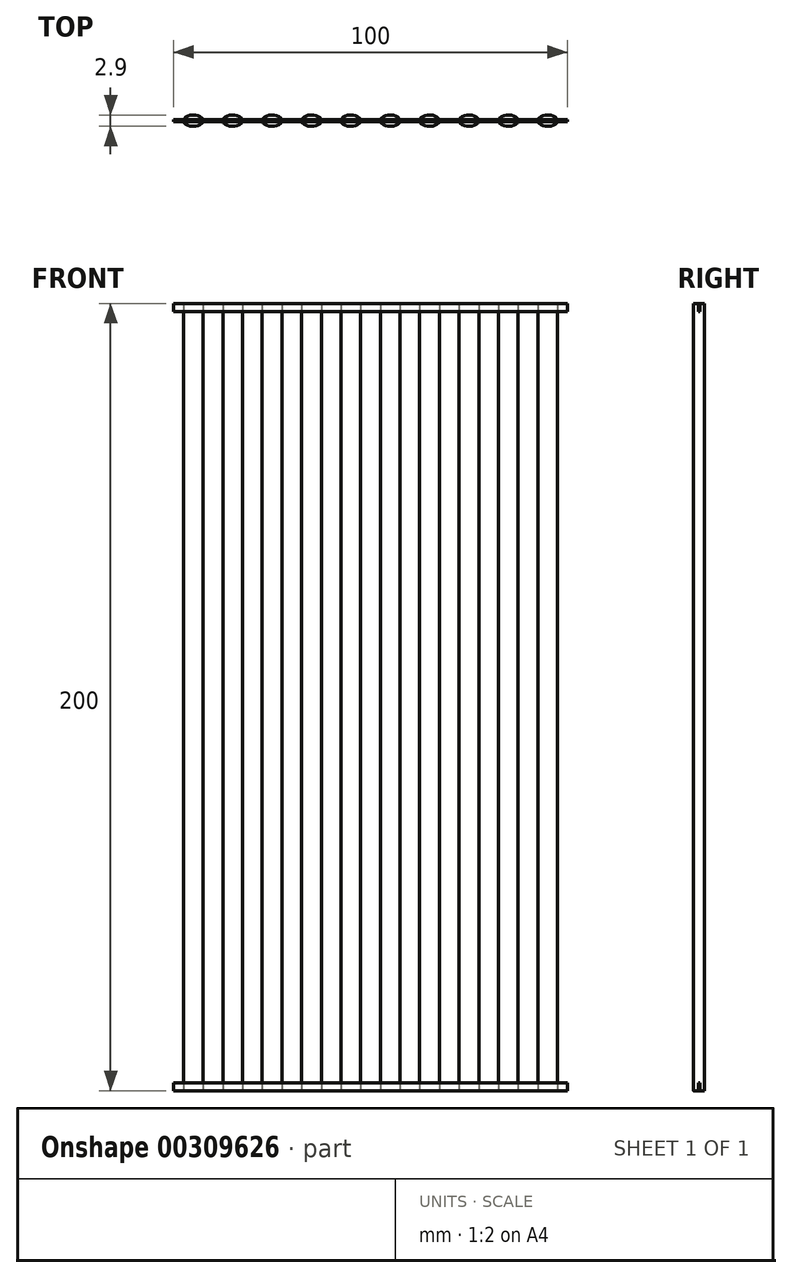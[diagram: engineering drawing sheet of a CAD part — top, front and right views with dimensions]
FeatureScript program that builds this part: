
annotation { "Feature Type Name" : "Feature", "Feature Type Description" : "" }
export const myFeature = defineFeature(function(context is Context, id is Id, definition is map)
    precondition{}
    {
        {
            var Q0;
            Q0=qCreatedBy(makeId("Top.planeOp"),FACE);
            var sketch = newSketch(context, id + "F0", { "sketchPlane" : qUnion([Q0])});
            skEllipse(sketch, "E0", {"center": v(-5, 0) * mm, "majorRadius": 2.5 * mm, "minorRadius": 1.45 * mm, "majorAxis": v(1, 0)});
            skEllipse(sketch, "E1", {"center": v(-15, 0) * mm, "majorRadius": 2.5 * mm, "minorRadius": 1.45 * mm, "majorAxis": v(1, 0)});
            skEllipse(sketch, "E2", {"center": v(-25, 0) * mm, "majorRadius": 2.5 * mm, "minorRadius": 1.45 * mm, "majorAxis": v(1, 0)});
            skEllipse(sketch, "E3", {"center": v(-35, 0) * mm, "majorRadius": 2.5 * mm, "minorRadius": 1.45 * mm, "majorAxis": v(1, 0)});
            skEllipse(sketch, "E4", {"center": v(-45, 0) * mm, "majorRadius": 2.5 * mm, "minorRadius": 1.45 * mm, "majorAxis": v(1, 0)});
            skSolve(sketch);
        }
        {
            var Q0;
            Q0=makeQuery(id+"F0.imprint","IMPRINT",FACE,{"disambiguationData":[TD([[makeQuery(id+"F0.imprint","IMPRINT",EDGE,{"derivedFrom":sQuery(id+"F0.wireOp",EDGE,"E4")}),1.0]])]});
            var Q1;
            Q1=makeQuery(id+"F0.imprint","IMPRINT",FACE,{"disambiguationData":[TD([[makeQuery(id+"F0.imprint","IMPRINT",EDGE,{"derivedFrom":sQuery(id+"F0.wireOp",EDGE,"E3")}),1.0]])]});
            var Q2;
            Q2=makeQuery(id+"F0.imprint","IMPRINT",FACE,{"disambiguationData":[TD([[makeQuery(id+"F0.imprint","IMPRINT",EDGE,{"derivedFrom":sQuery(id+"F0.wireOp",EDGE,"E2")}),1.0]])]});
            var Q3;
            Q3=makeQuery(id+"F0.imprint","IMPRINT",FACE,{"disambiguationData":[TD([[makeQuery(id+"F0.imprint","IMPRINT",EDGE,{"derivedFrom":sQuery(id+"F0.wireOp",EDGE,"E1")}),1.0]])]});
            var Q4;
            Q4=makeQuery(id+"F0.imprint","IMPRINT",FACE,{"disambiguationData":[TD([[makeQuery(id+"F0.imprint","IMPRINT",EDGE,{"derivedFrom":sQuery(id+"F0.wireOp",EDGE,"E0")}),1.0]])]});
            extrude(context, id + "F1", {"entities" : qUnion([Q0, Q1, Q2, Q3, Q4]), "endBound" : BoundingType.SYMMETRIC, "depth" : 200 * mm});
        }
        {
            var Q0;
            Q0=makeQuery(id+"F1.opExtrude","SWEPT_BODY",BODY,{"disambiguationData":[OSD([sQuery(id+"F0.wireOp",EDGE,"E4")])]});
            var Q1;
            Q1=makeQuery(id+"F1.opExtrude","SWEPT_BODY",BODY,{"disambiguationData":[OSD([sQuery(id+"F0.wireOp",EDGE,"E3")])]});
            var Q2;
            Q2=makeQuery(id+"F1.opExtrude","SWEPT_BODY",BODY,{"disambiguationData":[OSD([sQuery(id+"F0.wireOp",EDGE,"E2")])]});
            var Q3;
            Q3=makeQuery(id+"F1.opExtrude","SWEPT_BODY",BODY,{"disambiguationData":[OSD([sQuery(id+"F0.wireOp",EDGE,"E1")])]});
            var Q4;
            Q4=makeQuery(id+"F1.opExtrude","SWEPT_BODY",BODY,{"disambiguationData":[OSD([sQuery(id+"F0.wireOp",EDGE,"E0")])]});
            var Q5;
            Q5=qCreatedBy(makeId("Right.planeOp"),FACE);
            mirror(context, id + "F2", {"entities" : qUnion([Q0, Q1, Q2, Q3, Q4]), "mirrorPlane" : qUnion([Q5])});
        }
        {
            var Q0;
            Q0=qCreatedBy(makeId("Front.planeOp"),FACE);
            var sketch = newSketch(context, id + "F3", { "sketchPlane" : qUnion([Q0])});
            skPoint(sketch, "E5.middle", {"position": v(0, 0) * mm});
            skLineSegment(sketch, "E6.bottom", {"start": v(50, 98) * mm, "end": v(-50, 98) * mm});
            skLineSegment(sketch, "E6.top", {"start": v(50, 100) * mm, "end": v(-50, 100) * mm});
            skLineSegment(sketch, "E6.left", {"start": v(50, 98) * mm, "end": v(50, 100) * mm});
            skLineSegment(sketch, "E6.right", {"start": v(-50, 98) * mm, "end": v(-50, 100) * mm});
            skPoint(sketch, "E6.middle", {"position": v(0, 99) * mm});
            skLineSegment(sketch, "E7.bottom", {"start": v(50, -100) * mm, "end": v(-50, -100) * mm});
            skLineSegment(sketch, "E7.top", {"start": v(50, -98) * mm, "end": v(-50, -98) * mm});
            skLineSegment(sketch, "E7.left", {"start": v(50, -100) * mm, "end": v(50, -98) * mm});
            skLineSegment(sketch, "E7.right", {"start": v(-50, -100) * mm, "end": v(-50, -98) * mm});
            skPoint(sketch, "E7.middle", {"position": v(0, -99) * mm});
            skSolve(sketch);
        }
        {
            var Q0;
            Q0=makeQuery(id+"F3.imprint","IMPRINT",FACE,{"disambiguationData":[TD([[makeQuery(id+"F3.imprint","IMPRINT",EDGE,{"derivedFrom":sQuery(id+"F3.wireOp",EDGE,"E6.bottom")}),-1.0]])]});
            var Q1;
            Q1=makeQuery(id+"F3.imprint","IMPRINT",FACE,{"disambiguationData":[TD([[makeQuery(id+"F3.imprint","IMPRINT",EDGE,{"derivedFrom":sQuery(id+"F3.wireOp",EDGE,"E7.bottom")}),-1.0]])]});
            extrude(context, id + "F4", {"entities" : qUnion([Q0, Q1]), "endBound" : BoundingType.SYMMETRIC, "depth" : 0.4 * mm});
        }
    });
